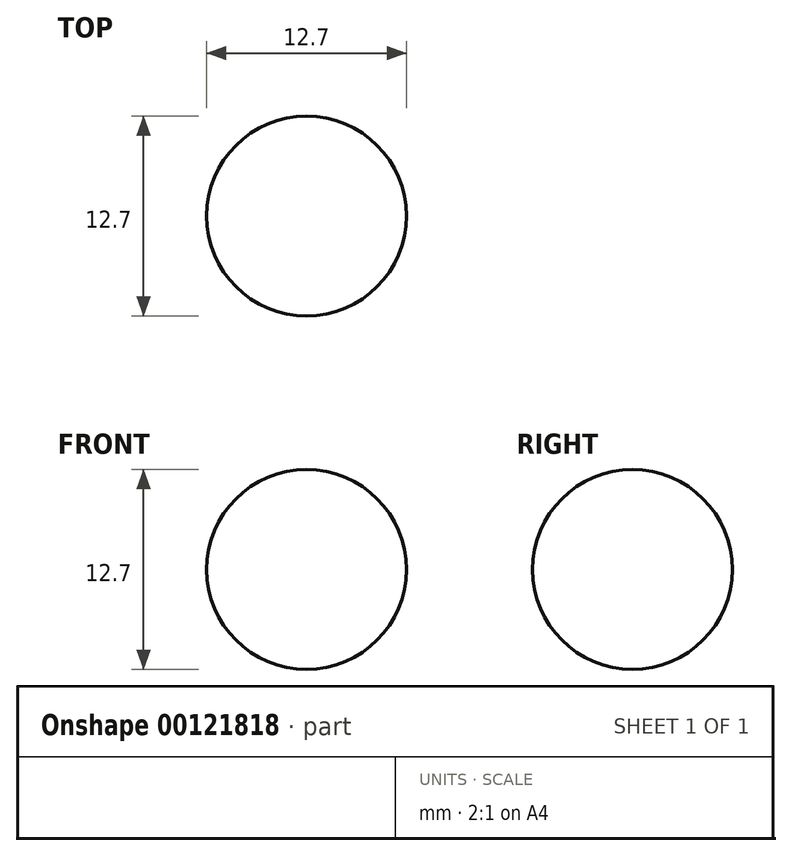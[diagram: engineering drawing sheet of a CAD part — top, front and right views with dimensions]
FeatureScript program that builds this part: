
annotation { "Feature Type Name" : "Feature", "Feature Type Description" : "" }
export const myFeature = defineFeature(function(context is Context, id is Id, definition is map)
    precondition{}
    {
        {
            var Q0;
            Q0=qCreatedBy(makeId("Front.planeOp"),FACE);
            var sketch = newSketch(context, id + "F0", { "sketchPlane" : qUnion([Q0])});
            skLineSegment(sketch, "E0", {"start": v(0, 0) * mm, "end": v(-12.7, 0) * mm});
            skArc(sketch, "E1", {"start": v(-12.7, 0) * mm, "mid": v(-6.35, 6.35) * mm, "end": v(0, 0) * mm});
            skSolve(sketch);
        }
        {
            var Q0;
            Q0 = qSketchRegion(id + "F0", true);
            var Q1;
            Q1=sQuery(id+"F0.wireOp",EDGE,"E0");
            revolve(context, id + "F1", {"entities" : qUnion([Q0]), "axis" : qUnion([Q1]), "revolveType" : RevolveType.FULL});
        }
    });
